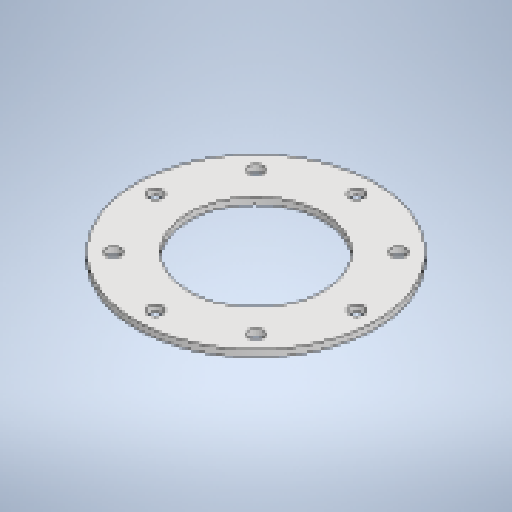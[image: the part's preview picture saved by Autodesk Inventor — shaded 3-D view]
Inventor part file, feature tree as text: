
AUTODESK INVENTOR PART (.ipt)
format: ipt  version: 2025.1 (Build 291241020, 241B)  size: 209,408 bytes
history: native  units: mm
features: other x3, sketch x2, sheet_metal_op x1, pattern_circular x1
ambient origin geometry x8: Origin, YZ Plane, XZ Plane, XY Plane, X Axis, Y Axis, Z Axis, Center Point
bodies: Body1 (feature_tree)
feature tree (7):
  sheet_metal_op  "Face2"
  pattern_circular  "Circular Pattern1"  [2 undecoded]
  sketch  "Sketch2"  dims[d14=8.0mm]
  other  "Plate2"
  sketch  "Sketch3"  dims[d15=17.0mm d17=8.0mm d18=0.0mm d19=80.0mm d20=360.0deg d25=161.0mm d27=285.0mm d28=240.0mm]
  other  "Cut1"
  other  "Definition1"
note: 2 required parameter values undecoded (feature->parameter linkage not recoverable at this tier; creation-order binding heuristic only, values carry confidence <= 0.55)
